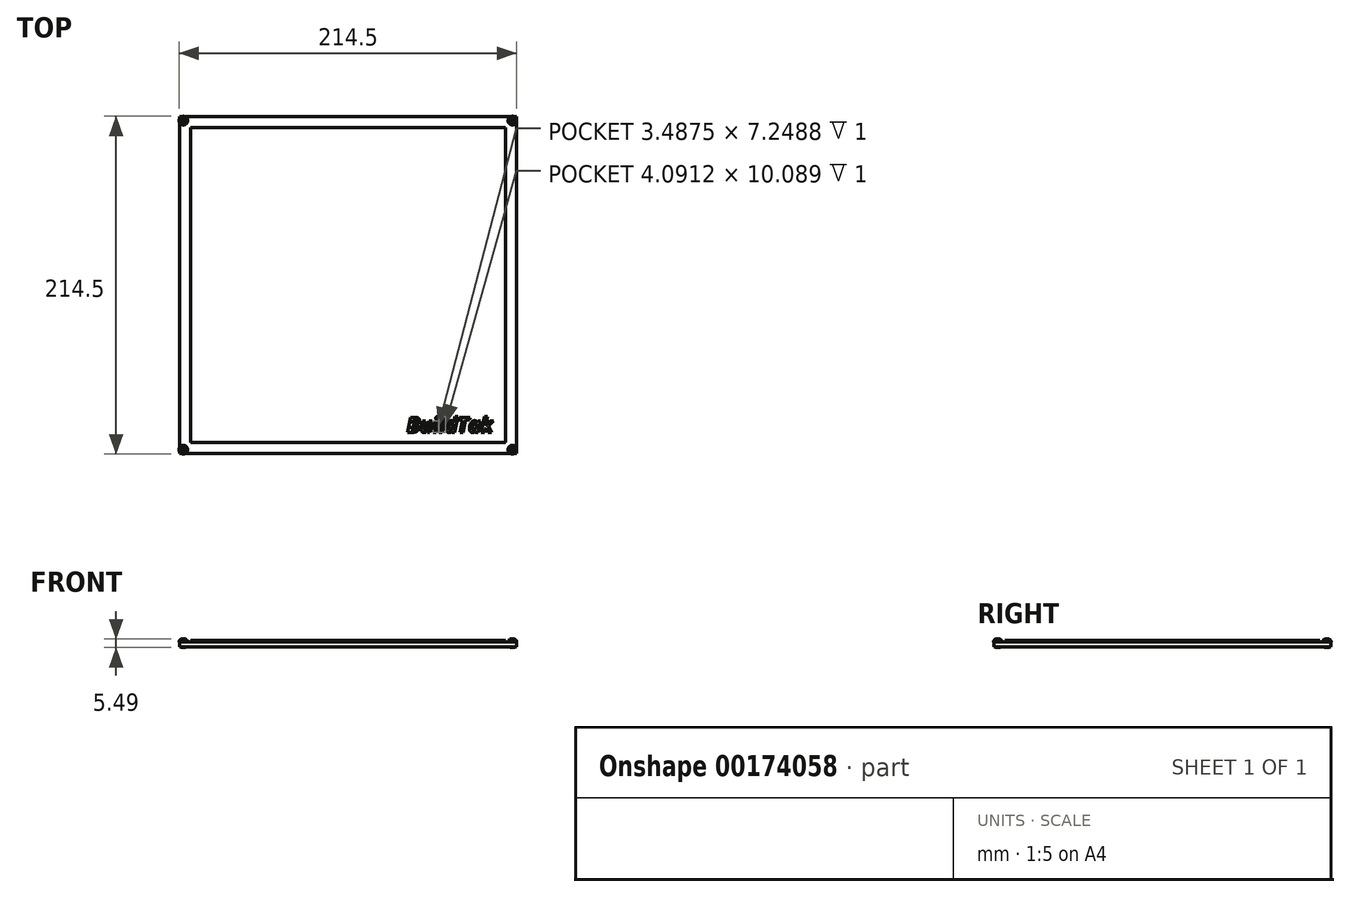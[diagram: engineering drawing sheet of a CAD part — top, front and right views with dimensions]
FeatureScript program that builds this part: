
annotation { "Feature Type Name" : "Feature", "Feature Type Description" : "" }
export const myFeature = defineFeature(function(context is Context, id is Id, definition is map)
    precondition{}
    {
        {
            var Q0;
            Q0=qCreatedBy(makeId("Top.planeOp"),FACE);
            var sketch = newSketch(context, id + "F0", { "sketchPlane" : qUnion([Q0])});
            skLineSegment(sketch, "E0.bottom", {"start": v(107, -107) * mm, "end": v(-107, -107) * mm});
            skLineSegment(sketch, "E0.top", {"start": v(107, 107) * mm, "end": v(-107, 107) * mm});
            skLineSegment(sketch, "E0.left", {"start": v(107, -107) * mm, "end": v(107, 107) * mm});
            skLineSegment(sketch, "E0.right", {"start": v(-107, -107) * mm, "end": v(-107, 107) * mm});
            skPoint(sketch, "E0.middle", {"position": v(0, 0) * mm});
            skCircle(sketch, "E1", {"center": v(-104.5, 104.5) * mm, "radius": 1.5 * mm});
            skLineSegment(sketch, "E2", {"start": v(0, -107) * mm, "end": v(0, 107) * mm, "construction": true});
            skLineSegment(sketch, "E3", {"start": v(-107, 0) * mm, "end": v(107, 0) * mm, "construction": true});
            skCircle(sketch, "E4.MirrorC", {"center": v(104.5, 104.5) * mm, "radius": 1.5 * mm});
            skCircle(sketch, "E5.MirrorC", {"center": v(104.5, -104.5) * mm, "radius": 1.5 * mm});
            skCircle(sketch, "E6.MirrorC", {"center": v(-104.5, -104.5) * mm, "radius": 1.5 * mm});
            skSolve(sketch);
        }
        {
            var Q0;
            Q0 = qSketchRegion(id + "F0", true);
            extrude(context, id + "F1", {"entities" : qUnion([Q0]), "depth" : 3 * mm});
        }
        {
            var Q0;
            Q0=makeQuery(id+"F1.opExtrude","CAP_FACE",FACE,{"disambiguationData":[OSD([sQuery(id+"F0.wireOp",EDGE,"E0.bottom"),sQuery(id+"F0.wireOp",EDGE,"E0.top"),sQuery(id+"F0.wireOp",EDGE,"E0.left"),sQuery(id+"F0.wireOp",EDGE,"E0.right"),sQuery(id+"F0.wireOp",EDGE,"E1"),sQuery(id+"F0.wireOp",EDGE,"E4.MirrorC"),sQuery(id+"F0.wireOp",EDGE,"E5.MirrorC"),sQuery(id+"F0.wireOp",EDGE,"E6.MirrorC")])],"isStart":false});
            var sketch = newSketch(context, id + "F2", { "sketchPlane" : qUnion([Q0])});
            skLineSegment(sketch, "E7.bottom", {"start": v(100, -100) * mm, "end": v(-100, -100) * mm});
            skLineSegment(sketch, "E7.top", {"start": v(100, 100) * mm, "end": v(-100, 100) * mm});
            skLineSegment(sketch, "E7.left", {"start": v(100, -100) * mm, "end": v(100, 100) * mm});
            skLineSegment(sketch, "E7.right", {"start": v(-100, -100) * mm, "end": v(-100, 100) * mm});
            skPoint(sketch, "E7.middle", {"position": v(0, 0) * mm});
            skSolve(sketch);
        }
        {
            var Q0;
            Q0 = qSketchRegion(id + "F2", true);
            extrude(context, id + "F3", {"entities" : qUnion([Q0]), "operationType" : NewBodyOperationType.ADD, "depth" : 1 * mm});
        }
        {
            var Q0;
            Q0=makeQuery(id+"F3.opExtrude","CAP_FACE",FACE,{"disambiguationData":[OSD([sQuery(id+"F2.wireOp",EDGE,"E7.bottom"),sQuery(id+"F2.wireOp",EDGE,"E7.top"),sQuery(id+"F2.wireOp",EDGE,"E7.left"),sQuery(id+"F2.wireOp",EDGE,"E7.right")])],"isStart":false});
            var sketch = newSketch(context, id + "F4", { "sketchPlane" : qUnion([Q0])});
            skText(sketch, "E8", { "text": "BuildTak", "fontName": "OpenSans-BoldItalic.ttf"});
            const initialGuessF4  = {"E8": [0.0375, -0.0935, 1, 0, 0.00956]};
            skSetInitialGuess(sketch, initialGuessF4);
            skSolve(sketch);
        }
        {
            var Q0;
            Q0 = qSketchRegion(id + "F4", true);
            extrude(context, id + "F5", {"entities" : qUnion([Q0]), "operationType" : NewBodyOperationType.REMOVE, "oppositeDirection" : true, "depth" : 1 * mm});
        }
        {
            var Q0;
            Q0=makeQuery(id+"F1.opExtrude","CAP_FACE",FACE,{"disambiguationData":[OSD([sQuery(id+"F0.wireOp",EDGE,"E0.bottom"),sQuery(id+"F0.wireOp",EDGE,"E0.top"),sQuery(id+"F0.wireOp",EDGE,"E0.left"),sQuery(id+"F0.wireOp",EDGE,"E0.right"),sQuery(id+"F0.wireOp",EDGE,"E1"),sQuery(id+"F0.wireOp",EDGE,"E4.MirrorC"),sQuery(id+"F0.wireOp",EDGE,"E5.MirrorC"),sQuery(id+"F0.wireOp",EDGE,"E6.MirrorC")])],"isStart":false});
            var sketch = newSketch(context, id + "F6", { "sketchPlane" : qUnion([Q0])});
            skCircle(sketch, "E9", {"center": v(-104.5, 104.5) * mm, "radius": 2.75 * mm});
            skCircle(sketch, "E10.0", {"center": v(-104.5, 104.5) * mm, "radius": 1.5 * mm});
            skLineSegment(sketch, "E11", {"start": v(0, -107) * mm, "end": v(0, 107) * mm, "construction": true});
            skLineSegment(sketch, "E12", {"start": v(-107, 0) * mm, "end": v(107, 0) * mm, "construction": true});
            skCircle(sketch, "E13.MirrorC", {"center": v(104.5, 104.5) * mm, "radius": 2.75 * mm});
            skCircle(sketch, "E14.MirrorC", {"center": v(104.5, -104.5) * mm, "radius": 2.75 * mm});
            skCircle(sketch, "E15.MirrorC", {"center": v(-104.5, -104.5) * mm, "radius": 2.75 * mm});
            skSolve(sketch);
        }
        {
            var Q0;
            Q0 = qSketchRegion(id + "F6", true);
            var Q1;
            Q1=makeQuery(id+"F6.imprint","IMPRINT",FACE,{"disambiguationData":[TD([[makeQuery(id+"F6.imprint","IMPRINT",EDGE,{"derivedFrom":sQuery(id+"F6.wireOp",EDGE,"E10.0")}),1.0]])]});
            extrude(context, id + "F7", {"entities" : qUnion([Q0, Q1]), "operationType" : NewBodyOperationType.ADD, "depth" : 2 * mm});
        }
        {
            var Q0;
            Q0=makeQuery(id+"F7.opExtrude","CAP_FACE",FACE,{"disambiguationData":[OSD([sQuery(id+"F6.wireOp",EDGE,"E9")])],"isStart":false});
            var sketch = newSketch(context, id + "F8", { "sketchPlane" : qUnion([Q0])});
            skCircle(sketch, "E16.cCircle", {"center": v(-104.5, 104.5) * mm, "radius": 1 * mm, "construction": true});
            skLineSegment(sketch, "E16.0", {"start": v(-103.49, 103.95) * mm, "end": v(-104.47, 103.35) * mm});
            skLineSegment(sketch, "E16.1", {"start": v(-104.47, 103.35) * mm, "end": v(-105.49, 103.9) * mm});
            skLineSegment(sketch, "E16.2", {"start": v(-105.49, 103.9) * mm, "end": v(-105.51, 105.05) * mm});
            skLineSegment(sketch, "E16.3", {"start": v(-105.51, 105.05) * mm, "end": v(-104.53, 105.65) * mm});
            skLineSegment(sketch, "E16.4", {"start": v(-104.53, 105.65) * mm, "end": v(-103.51, 105.1) * mm});
            skLineSegment(sketch, "E16.5", {"start": v(-103.51, 105.1) * mm, "end": v(-103.49, 103.95) * mm});
            skPoint(sketch, "E16.0.midPoint", {"position": v(-103.98, 103.65) * mm});
            skSolve(sketch);
        }
        {
            var Q0;
            Q0=makeQuery(id+"F7.opExtrude","CAP_FACE",FACE,{"disambiguationData":[OSD([sQuery(id+"F6.wireOp",EDGE,"E13.MirrorC")])],"isStart":false});
            var sketch = newSketch(context, id + "F9", { "sketchPlane" : qUnion([Q0])});
            skCircle(sketch, "E17.cCircle", {"center": v(104.5, 104.5) * mm, "radius": 1 * mm, "construction": true});
            skLineSegment(sketch, "E17.0", {"start": v(105.5, 103.93) * mm, "end": v(104.51, 103.35) * mm});
            skLineSegment(sketch, "E17.1", {"start": v(104.51, 103.35) * mm, "end": v(103.5, 103.91) * mm});
            skLineSegment(sketch, "E17.2", {"start": v(103.5, 103.91) * mm, "end": v(103.5, 105.07) * mm});
            skLineSegment(sketch, "E17.3", {"start": v(103.5, 105.07) * mm, "end": v(104.49, 105.65) * mm});
            skLineSegment(sketch, "E17.4", {"start": v(104.49, 105.65) * mm, "end": v(105.5, 105.09) * mm});
            skLineSegment(sketch, "E17.5", {"start": v(105.5, 105.09) * mm, "end": v(105.5, 103.93) * mm});
            skPoint(sketch, "E17.0.midPoint", {"position": v(105, 103.64) * mm});
            skSolve(sketch);
        }
        {
            var Q0;
            Q0=makeQuery(id+"F7.opExtrude","CAP_FACE",FACE,{"disambiguationData":[OSD([sQuery(id+"F6.wireOp",EDGE,"E15.MirrorC")])],"isStart":false});
            var sketch = newSketch(context, id + "F10", { "sketchPlane" : qUnion([Q0])});
            skCircle(sketch, "E18.cCircle", {"center": v(-104.5, -104.5) * mm, "radius": 1 * mm, "construction": true});
            skLineSegment(sketch, "E18.0", {"start": v(-103.47, -105.03) * mm, "end": v(-104.45, -105.65) * mm});
            skLineSegment(sketch, "E18.1", {"start": v(-104.45, -105.65) * mm, "end": v(-105.47, -105.12) * mm});
            skLineSegment(sketch, "E18.2", {"start": v(-105.47, -105.12) * mm, "end": v(-105.53, -103.97) * mm});
            skLineSegment(sketch, "E18.3", {"start": v(-105.53, -103.97) * mm, "end": v(-104.55, -103.35) * mm});
            skLineSegment(sketch, "E18.4", {"start": v(-104.55, -103.35) * mm, "end": v(-103.53, -103.88) * mm});
            skLineSegment(sketch, "E18.5", {"start": v(-103.53, -103.88) * mm, "end": v(-103.47, -105.03) * mm});
            skPoint(sketch, "E18.0.midPoint", {"position": v(-103.96, -105.34) * mm});
            skSolve(sketch);
        }
        {
            var Q0;
            Q0=makeQuery(id+"F7.opExtrude","CAP_FACE",FACE,{"disambiguationData":[OSD([sQuery(id+"F6.wireOp",EDGE,"E14.MirrorC")])],"isStart":false});
            var sketch = newSketch(context, id + "F11", { "sketchPlane" : qUnion([Q0])});
            skCircle(sketch, "E19.cCircle", {"center": v(104.5, -104.5) * mm, "radius": 1 * mm, "construction": true});
            skLineSegment(sketch, "E19.0", {"start": v(105.5, -105.08) * mm, "end": v(104.5, -105.65) * mm});
            skLineSegment(sketch, "E19.1", {"start": v(104.5, -105.65) * mm, "end": v(103.5, -105.08) * mm});
            skLineSegment(sketch, "E19.2", {"start": v(103.5, -105.08) * mm, "end": v(103.5, -103.92) * mm});
            skLineSegment(sketch, "E19.3", {"start": v(103.5, -103.92) * mm, "end": v(104.5, -103.35) * mm});
            skLineSegment(sketch, "E19.4", {"start": v(104.5, -103.35) * mm, "end": v(105.5, -103.92) * mm});
            skLineSegment(sketch, "E19.5", {"start": v(105.5, -103.92) * mm, "end": v(105.5, -105.08) * mm});
            skPoint(sketch, "E19.0.midPoint", {"position": v(105, -105.37) * mm});
            skSolve(sketch);
        }
        {
            var Q0;
            Q0 = qSketchRegion(id + "F11", true);
            var Q1;
            Q1 = qSketchRegion(id + "F10", true);
            var Q2;
            Q2 = qSketchRegion(id + "F9", true);
            var Q3;
            Q3 = qSketchRegion(id + "F8", true);
            extrude(context, id + "F12", {"entities" : qUnion([Q0, Q1, Q2, Q3]), "operationType" : NewBodyOperationType.REMOVE, "oppositeDirection" : true, "depth" : 1 * mm});
        }
        {
            var Q0;
            Q0=makeQuery(id+"F7.opExtrude","CAP_EDGE",EDGE,{"disambiguationData":[OSD([sQuery(id+"F6.wireOp",EDGE,"E9")])],"isStart":false});
            var Q1;
            Q1=makeQuery(id+"F7.opExtrude","CAP_EDGE",EDGE,{"disambiguationData":[OSD([sQuery(id+"F6.wireOp",EDGE,"E13.MirrorC")])],"isStart":false});
            var Q2;
            Q2=makeQuery(id+"F7.opExtrude","CAP_EDGE",EDGE,{"disambiguationData":[OSD([sQuery(id+"F6.wireOp",EDGE,"E14.MirrorC")])],"isStart":false});
            var Q3;
            Q3=makeQuery(id+"F7.opExtrude","CAP_EDGE",EDGE,{"disambiguationData":[OSD([sQuery(id+"F6.wireOp",EDGE,"E15.MirrorC")])],"isStart":false});
            fillet(context, id + "F13", {"entities" : qUnion([Q0, Q1, Q2, Q3]), "radius" : 2 * mm, "tangentPropagation" : true, "allowEdgeOverflow" : false});
        }
        {
            var Q0;
            Q0=makeQuery(id+"F7.boolean.opBoolean","SPLIT",FACE,{"disambiguationData":[TD([makeQuery(id+"F1.opExtrude","SWEPT_FACE",FACE,{"disambiguationData":[OSD([sQuery(id+"F0.wireOp",EDGE,"E6.MirrorC")])]})])],"derivedFrom":makeQuery(id+"F7.opExtrude","CAP_FACE",FACE,{"disambiguationData":[OSD([sQuery(id+"F6.wireOp",EDGE,"E15.MirrorC")])],"isStart":true})});
            var Q1;
            Q1=makeQuery(id+"F7.boolean.opBoolean","SPLIT",FACE,{"disambiguationData":[TD([makeQuery(id+"F1.opExtrude","SWEPT_FACE",FACE,{"disambiguationData":[OSD([sQuery(id+"F0.wireOp",EDGE,"E5.MirrorC")])]})])],"derivedFrom":makeQuery(id+"F7.opExtrude","CAP_FACE",FACE,{"disambiguationData":[OSD([sQuery(id+"F6.wireOp",EDGE,"E14.MirrorC")])],"isStart":true})});
            var Q2;
            Q2=makeQuery(id+"F7.boolean.opBoolean","SPLIT",FACE,{"disambiguationData":[TD([makeQuery(id+"F1.opExtrude","SWEPT_FACE",FACE,{"disambiguationData":[OSD([sQuery(id+"F0.wireOp",EDGE,"E4.MirrorC")])]})])],"derivedFrom":makeQuery(id+"F7.opExtrude","CAP_FACE",FACE,{"disambiguationData":[OSD([sQuery(id+"F6.wireOp",EDGE,"E13.MirrorC")])],"isStart":true})});
            var Q3;
            Q3=makeQuery(id+"F7.boolean.opBoolean","SPLIT",FACE,{"disambiguationData":[TD([makeQuery(id+"F1.opExtrude","SWEPT_FACE",FACE,{"disambiguationData":[OSD([sQuery(id+"F0.wireOp",EDGE,"E1")])]})])],"derivedFrom":makeQuery(id+"F7.opExtrude","CAP_FACE",FACE,{"disambiguationData":[OSD([sQuery(id+"F6.wireOp",EDGE,"E9")])],"isStart":true})});
            extrude(context, id + "F14", {"entities" : qUnion([Q0, Q1, Q2, Q3]), "operationType" : NewBodyOperationType.ADD, "depth" : 3.5 * mm});
        }
        {
            var Q0;
            Q0=qCreatedBy(makeId("Top.planeOp"),FACE);
            var sketch = newSketch(context, id + "F15", { "sketchPlane" : qUnion([Q0])});
            skCircle(sketch, "E20", {"center": v(0, 0) * mm, "radius": 2 * mm});
            skSolve(sketch);
        }
        {
            var Q0;
            Q0 = qSketchRegion(id + "F15", true);
            extrude(context, id + "F16", {"entities" : qUnion([Q0]), "depth" : 25 * mm});
        }
        {
            var Q0;
            Q0=makeQuery(id+"F16.opExtrude","SWEPT_BODY",BODY,{"disambiguationData":[OSD([sQuery(id+"F15.wireOp",EDGE,"E20")])]});
            deleteBodies(context, id + "F17", {"entities" : qUnion([Q0])});
        }
    });
